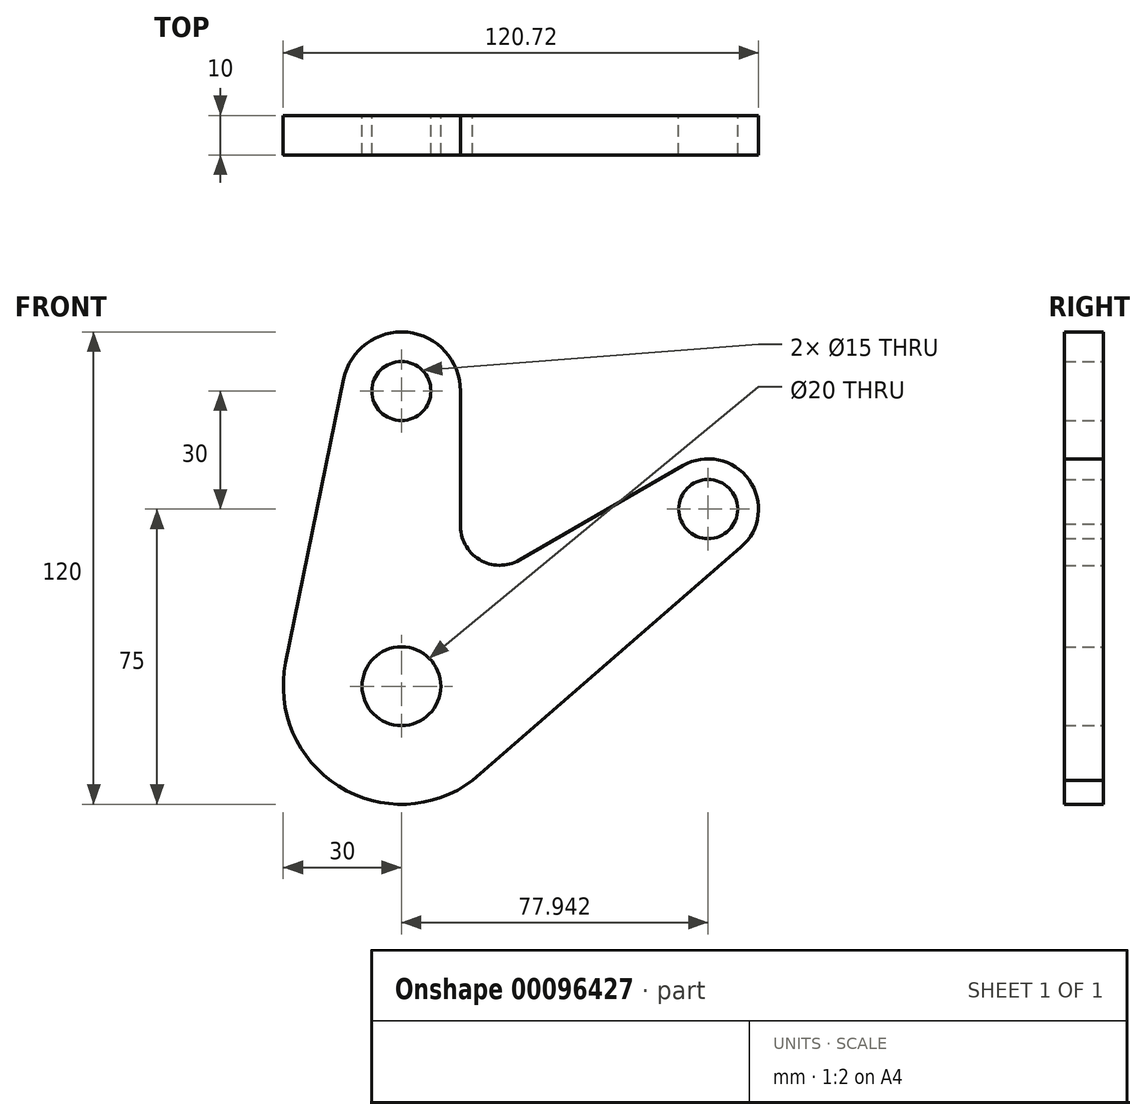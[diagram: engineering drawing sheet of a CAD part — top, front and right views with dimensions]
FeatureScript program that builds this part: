
annotation { "Feature Type Name" : "Feature", "Feature Type Description" : "" }
export const myFeature = defineFeature(function(context is Context, id is Id, definition is map)
    precondition{}
    {
        {
            var Q0;
            Q0=qCreatedBy(makeId("Front.planeOp"),FACE);
            var sketch = newSketch(context, id + "F0", { "sketchPlane" : qUnion([Q0])});
            skCircle(sketch, "E0", {"center": v(0, 0) * mm, "radius": 10 * mm});
            skArc(sketch, "E1", {"start": v(-29.4, 6) * mm, "mid": v(-16, -25.38) * mm, "end": v(18.1, -23.92) * mm});
            skCircle(sketch, "E2", {"center": v(0, 75) * mm, "radius": 7.5 * mm});
            skCircle(sketch, "E3", {"center": v(77.94, 45) * mm, "radius": 7.5 * mm});
            skArc(sketch, "E4", {"start": v(15, 75) * mm, "mid": v(1.5, 89.92) * mm, "end": v(-14.7, 78) * mm});
            skArc(sketch, "E5", {"start": v(86.32, 35.36) * mm, "mid": v(88.32, 52.46) * mm, "end": v(71.47, 56.02) * mm});
            skLineSegment(sketch, "E6", {"start": v(0, 75) * mm, "end": v(0, 0) * mm, "construction": true});
            skLineSegment(sketch, "E7", {"start": v(77.94, 45) * mm, "end": v(0, 0) * mm, "construction": true});
            skLineSegment(sketch, "E8", {"start": v(18.1, -23.92) * mm, "end": v(86.32, 35.36) * mm});
            skLineSegment(sketch, "E9", {"start": v(-29.4, 6) * mm, "end": v(-14.7, 78) * mm});
            skLineSegment(sketch, "E10", {"start": v(15, 75) * mm, "end": v(15, 41.16) * mm});
            skLineSegment(sketch, "E11", {"start": v(30, 32.07) * mm, "end": v(71.47, 56.02) * mm});
            skPoint(sketch, "E12.visualSharp", {"position": v(15, 26) * mm});
            skArc(sketch, "E12.filletArc", {"start": v(15, 41.16) * mm, "mid": v(19.8, 32.18) * mm, "end": v(30, 32.07) * mm});
            skSolve(sketch);
        }
        {
            var Q0;
            Q0 = qSketchRegion(id + "F0", true);
            extrude(context, id + "F1", {"entities" : qUnion([Q0]), "endBound" : BoundingType.SYMMETRIC, "depth" : 10 * mm});
        }
    });
